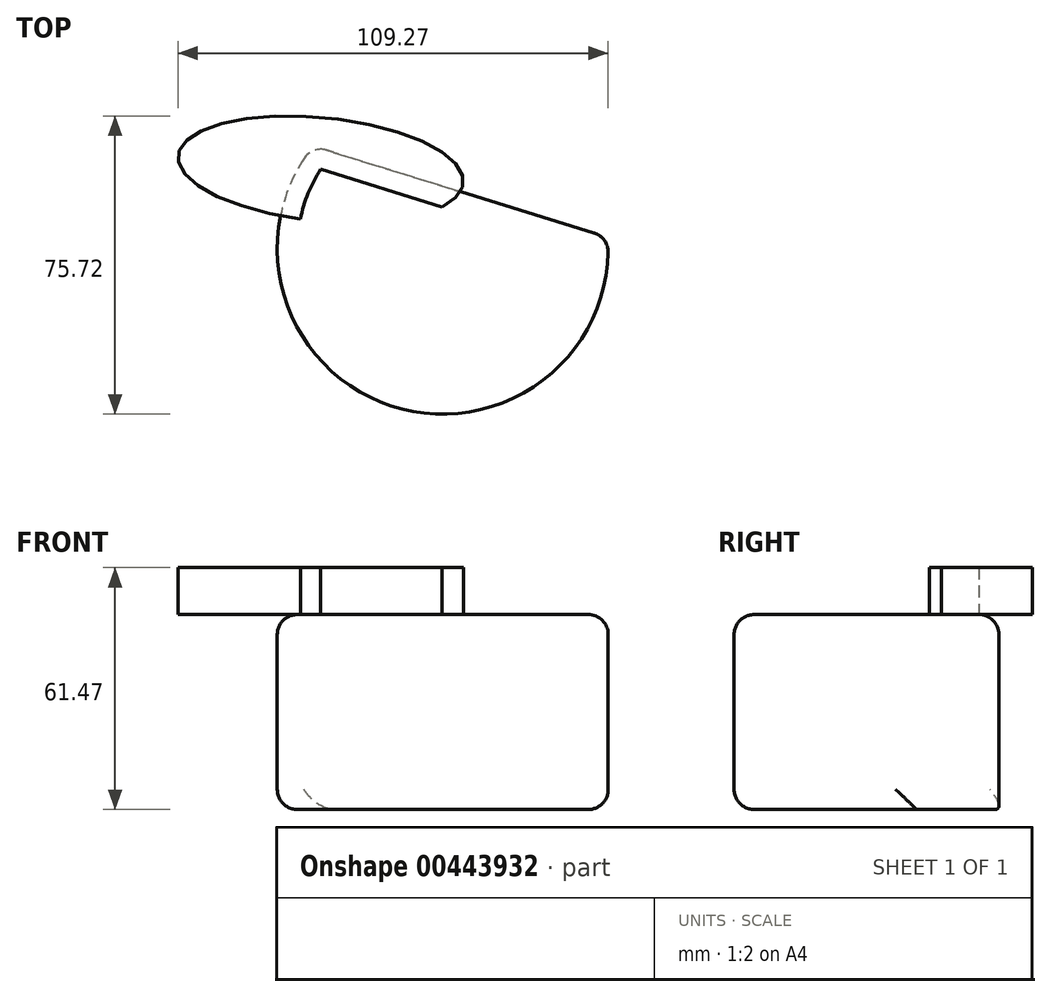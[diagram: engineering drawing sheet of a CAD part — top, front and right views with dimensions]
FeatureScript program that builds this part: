
annotation { "Feature Type Name" : "Feature", "Feature Type Description" : "" }
export const myFeature = defineFeature(function(context is Context, id is Id, definition is map)
    precondition{}
    {
        {
            var Q0;
            Q0=qCreatedBy(makeId("Top.planeOp"),FACE);
            var sketch = newSketch(context, id + "F0", { "sketchPlane" : qUnion([Q0])});
            skArc(sketch, "E0", {"start": v(-31.85, 32.62) * mm, "mid": v(-11.3, -33.62) * mm, "end": v(43.06, 9.43) * mm});
            skLineSegment(sketch, "E1", {"start": v(-31.85, 32.62) * mm, "end": v(43.06, 9.43) * mm});
            skSolve(sketch);
        }
        {
            var Q0;
            Q0=makeQuery(id+"F0.imprint","IMPRINT",FACE,{"disambiguationData":[TD([[makeQuery(id+"F0.imprint","IMPRINT",EDGE,{"derivedFrom":sQuery(id+"F0.wireOp",EDGE,"E0")}),1.0]])]});
            extrude(context, id + "F1", {"entities" : qUnion([Q0]), "depth" : 49.53 * mm});
        }
        {
            var Q0;
            Q0=makeQuery(id+"F1.opExtrude","SWEPT_FACE",FACE,{"disambiguationData":[OSD([sQuery(id+"F0.wireOp",EDGE,"E0")])]});
            var Q1;
            Q1=makeQuery(id+"F1.opExtrude","CAP_FACE",FACE,{"disambiguationData":[OSD([sQuery(id+"F0.wireOp",EDGE,"E0"),sQuery(id+"F0.wireOp",EDGE,"E1")])],"isStart":false});
            fillet(context, id + "F2", {"entities" : qUnion([Q0, Q1]), "radius" : 5.08 * mm, "tangentPropagation" : true, "allowEdgeOverflow" : false});
        }
        {
            var Q0;
            Q0=makeQuery(id+"F1.opExtrude","CAP_FACE",FACE,{"disambiguationData":[OSD([sQuery(id+"F0.wireOp",EDGE,"E0"),sQuery(id+"F0.wireOp",EDGE,"E1")])],"isStart":false});
            var sketch = newSketch(context, id + "F3", { "sketchPlane" : qUnion([Q0])});
            skEllipse(sketch, "E2", {"center": v(-29.86, 26.68) * mm, "majorRadius": 36.4 * mm, "minorRadius": 13.13 * mm, "majorAxis": v(1, -0.1)});
            skSolve(sketch);
        }
        {
            var Q0;
            {var subQ0=sQuery(id+"F3.wireOp",EDGE,"E2");var subQ1=sQuery(id+"F0.wireOp",EDGE,"E1");var subQ2=sQuery(id+"F0.wireOp",EDGE,"E0");var subQ3=makeQuery(id+"F1.opExtrude","CAP_FACE",FACE,{"disambiguationData":[OSD([subQ2,subQ1])],"isStart":false});var subQ4=makeQuery(id+"F2.opFillet","BLEND_EDGE",EDGE,{"blendedFrom":[makeQuery(id+"F1.opExtrude","CAP_EDGE",EDGE,{"disambiguationData":[OSD([subQ2])],"isStart":false}),subQ3],"blendedInto":[subQ3]});var subQ5=makeQuery(id+"F3.imprint","INTERSECT",VERTEX,{"derivedFrom":[subQ4,subQ0]});Q0=makeQuery(id+"F3.imprint","IMPRINT",FACE,{"disambiguationData":[TD([[makeQuery(id+"F3.imprint","IMPRINT",EDGE,{"disambiguationData":[TD([[subQ5,1.0]])],"derivedFrom":subQ0}),1.0]])]});}
            extrude(context, id + "F4", {"entities" : qUnion([Q0]), "depth" : 11.94 * mm});
        }
    });
